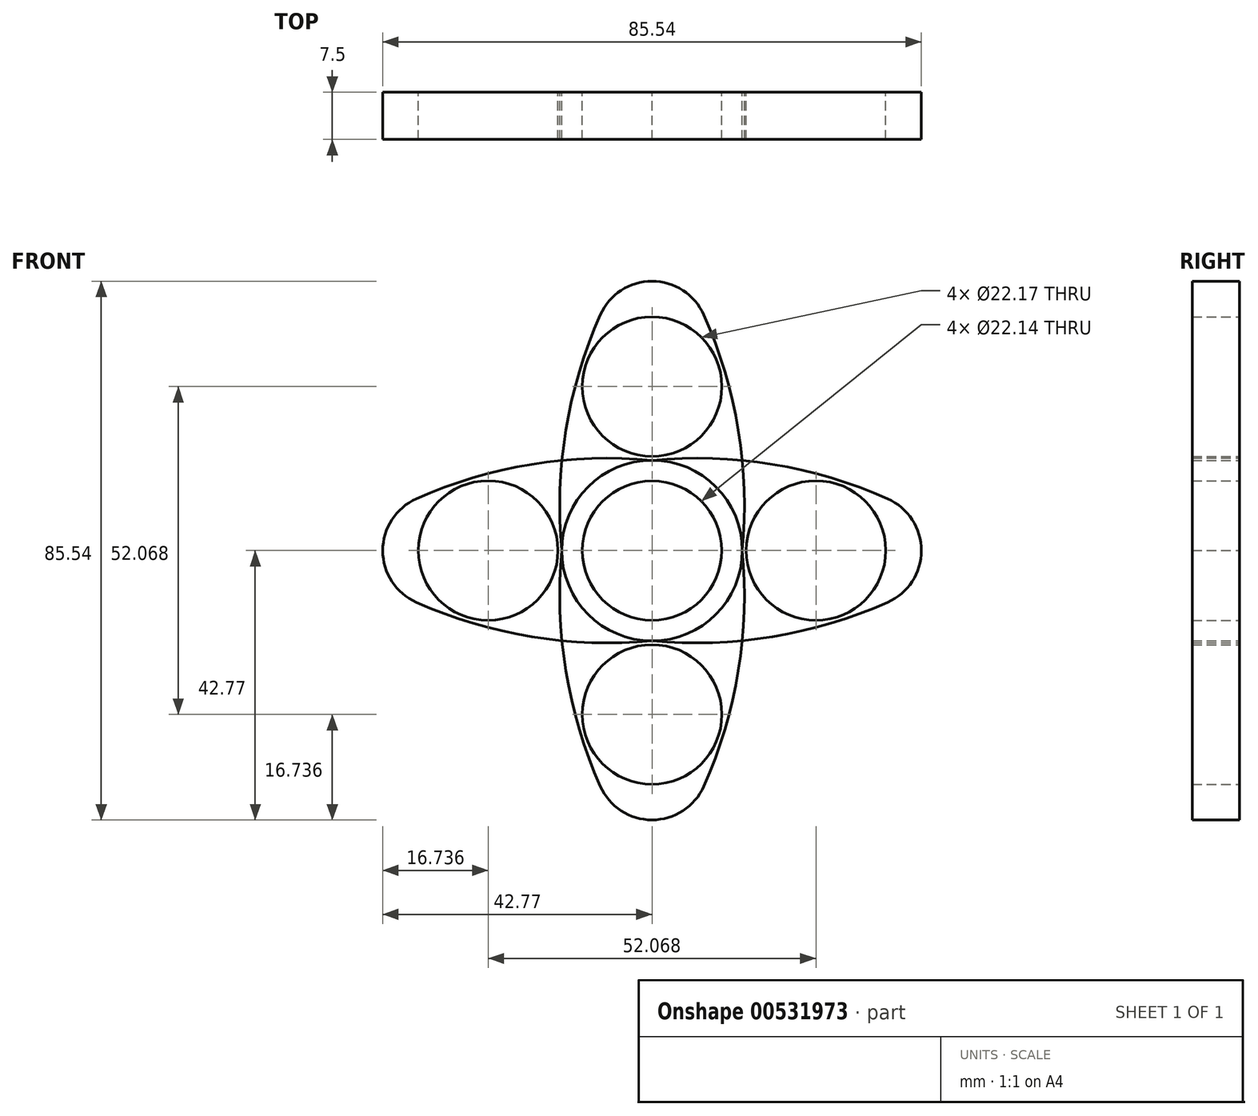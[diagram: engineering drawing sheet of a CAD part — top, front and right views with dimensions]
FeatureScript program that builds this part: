
annotation { "Feature Type Name" : "Feature", "Feature Type Description" : "" }
export const myFeature = defineFeature(function(context is Context, id is Id, definition is map)
    precondition{}
    {
        {
            var Q0;
            Q0=qCreatedBy(makeId("Front.planeOp"),FACE);
            var sketch = newSketch(context, id + "F0", { "sketchPlane" : qUnion([Q0])});
            skCircle(sketch, "E0", {"center": v(0, 0) * mm, "radius": 11.07 * mm});
            skCircle(sketch, "E1", {"center": v(0, 0) * mm, "radius": 14.34 * mm});
            skArc(sketch, "E2", {"start": v(0, 51.55) * mm, "mid": v(-11.93, 27.1) * mm, "end": v(-14.34, 0) * mm});
            skArc(sketch, "E3", {"start": v(14.34, 0) * mm, "mid": v(11.93, 27.1) * mm, "end": v(0, 51.55) * mm});
            skCircle(sketch, "E4", {"center": v(0, 26.03) * mm, "radius": 11.08 * mm});
            skSolve(sketch);
        }
        {
            var Q0;
            {var subQ0=sQuery(id+"F0.wireOp",EDGE,"E2");Q0=makeQuery(id+"F0.imprint","IMPRINT",FACE,{"disambiguationData":[TD([[makeQuery(id+"F0.imprint","IMPRINT",EDGE,{"derivedFrom":subQ0}),1.0]])]});}
            var Q1;
            Q1=makeQuery(id+"F0.imprint","IMPRINT",FACE,{"disambiguationData":[TD([[makeQuery(id+"F0.imprint","IMPRINT",EDGE,{"derivedFrom":sQuery(id+"F0.wireOp",EDGE,"E0")}),-1.0]])]});
            extrude(context, id + "F1", {"entities" : qUnion([Q0, Q1]), "depth" : 7.5 * mm, "offsetDistance" : 25 * mm});
        }
        {
            var Q0;
            Q0=makeQuery(id+"F1.opExtrude","SWEPT_BODY",BODY,{"disambiguationData":[OSD([sQuery(id+"F0.wireOp",EDGE,"E0"),sQuery(id+"F0.wireOp",EDGE,"E1"),sQuery(id+"F0.wireOp",EDGE,"E2"),sQuery(id+"F0.wireOp",EDGE,"E3"),sQuery(id+"F0.wireOp",EDGE,"E4")])]});
            var Q1;
            Q1=makeQuery(id+"F1.opExtrude","CAP_EDGE",EDGE,{"disambiguationData":[OSD([sQuery(id+"F0.wireOp",EDGE,"E0")])],"isStart":false});
            transform(context, id + "F2", {"entities" : qUnion([Q0]), "transformType" : TransformType.ROTATION, "transformAxis" : qUnion([Q1]), "angle" : 90 * degree, "makeCopy" : true});
        }
        {
            var Q0;
            Q0=makeQuery(id+"F2.opPattern","COPY",BODY,{"derivedFrom":makeQuery(id+"F1.opExtrude","SWEPT_BODY",BODY,{"disambiguationData":[OSD([sQuery(id+"F0.wireOp",EDGE,"E0"),sQuery(id+"F0.wireOp",EDGE,"E1"),sQuery(id+"F0.wireOp",EDGE,"E2"),sQuery(id+"F0.wireOp",EDGE,"E3"),sQuery(id+"F0.wireOp",EDGE,"E4")])]}),"instanceName":"1"});
            var Q1;
            Q1=makeQuery(id+"F1.opExtrude","CAP_EDGE",EDGE,{"disambiguationData":[OSD([sQuery(id+"F0.wireOp",EDGE,"E0")])],"isStart":false});
            transform(context, id + "F3", {"entities" : qUnion([Q0]), "transformType" : TransformType.ROTATION, "transformAxis" : qUnion([Q1]), "angle" : 90 * degree, "makeCopy" : true});
        }
        {
            var Q0;
            Q0=makeQuery(id+"F3.opPattern","COPY",BODY,{"derivedFrom":makeQuery(id+"F2.opPattern","COPY",BODY,{"derivedFrom":makeQuery(id+"F1.opExtrude","SWEPT_BODY",BODY,{"disambiguationData":[OSD([sQuery(id+"F0.wireOp",EDGE,"E0"),sQuery(id+"F0.wireOp",EDGE,"E1"),sQuery(id+"F0.wireOp",EDGE,"E2"),sQuery(id+"F0.wireOp",EDGE,"E3"),sQuery(id+"F0.wireOp",EDGE,"E4")])]}),"instanceName":"1"}),"instanceName":"1"});
            var Q1;
            Q1=makeQuery(id+"F1.opExtrude","CAP_EDGE",EDGE,{"disambiguationData":[OSD([sQuery(id+"F0.wireOp",EDGE,"E0")])],"isStart":false});
            transform(context, id + "F4", {"entities" : qUnion([Q0]), "transformType" : TransformType.ROTATION, "transformAxis" : qUnion([Q1]), "angle" : 90 * degree, "makeCopy" : true});
        }
        {
            var Q0;
            Q0=makeQuery(id+"F1.opExtrude","SWEPT_EDGE",EDGE,{"disambiguationData":[OSD([sQuery(id+"F0.wireOp",EDGE,"E2"),sQuery(id+"F0.wireOp",EDGE,"E3")])]});
            var Q1;
            Q1=makeQuery(id+"F4.opPattern","COPY",EDGE,{"derivedFrom":makeQuery(id+"F3.opPattern","COPY",EDGE,{"derivedFrom":makeQuery(id+"F2.opPattern","COPY",EDGE,{"derivedFrom":makeQuery(id+"F1.opExtrude","SWEPT_EDGE",EDGE,{"disambiguationData":[OSD([sQuery(id+"F0.wireOp",EDGE,"E2"),sQuery(id+"F0.wireOp",EDGE,"E3")])]}),"instanceName":"1"}),"instanceName":"1"}),"instanceName":"1"});
            var Q2;
            Q2=makeQuery(id+"F3.opPattern","COPY",EDGE,{"derivedFrom":makeQuery(id+"F2.opPattern","COPY",EDGE,{"derivedFrom":makeQuery(id+"F1.opExtrude","SWEPT_EDGE",EDGE,{"disambiguationData":[OSD([sQuery(id+"F0.wireOp",EDGE,"E2"),sQuery(id+"F0.wireOp",EDGE,"E3")])]}),"instanceName":"1"}),"instanceName":"1"});
            var Q3;
            Q3=makeQuery(id+"F2.opPattern","COPY",EDGE,{"derivedFrom":makeQuery(id+"F1.opExtrude","SWEPT_EDGE",EDGE,{"disambiguationData":[OSD([sQuery(id+"F0.wireOp",EDGE,"E2"),sQuery(id+"F0.wireOp",EDGE,"E3")])]}),"instanceName":"1"});
            fillet(context, id + "F5", {"entities" : qUnion([Q0, Q1, Q2, Q3]), "radius" : 9 * mm, "tangentPropagation" : true, "allowEdgeOverflow" : false});
        }
    });
